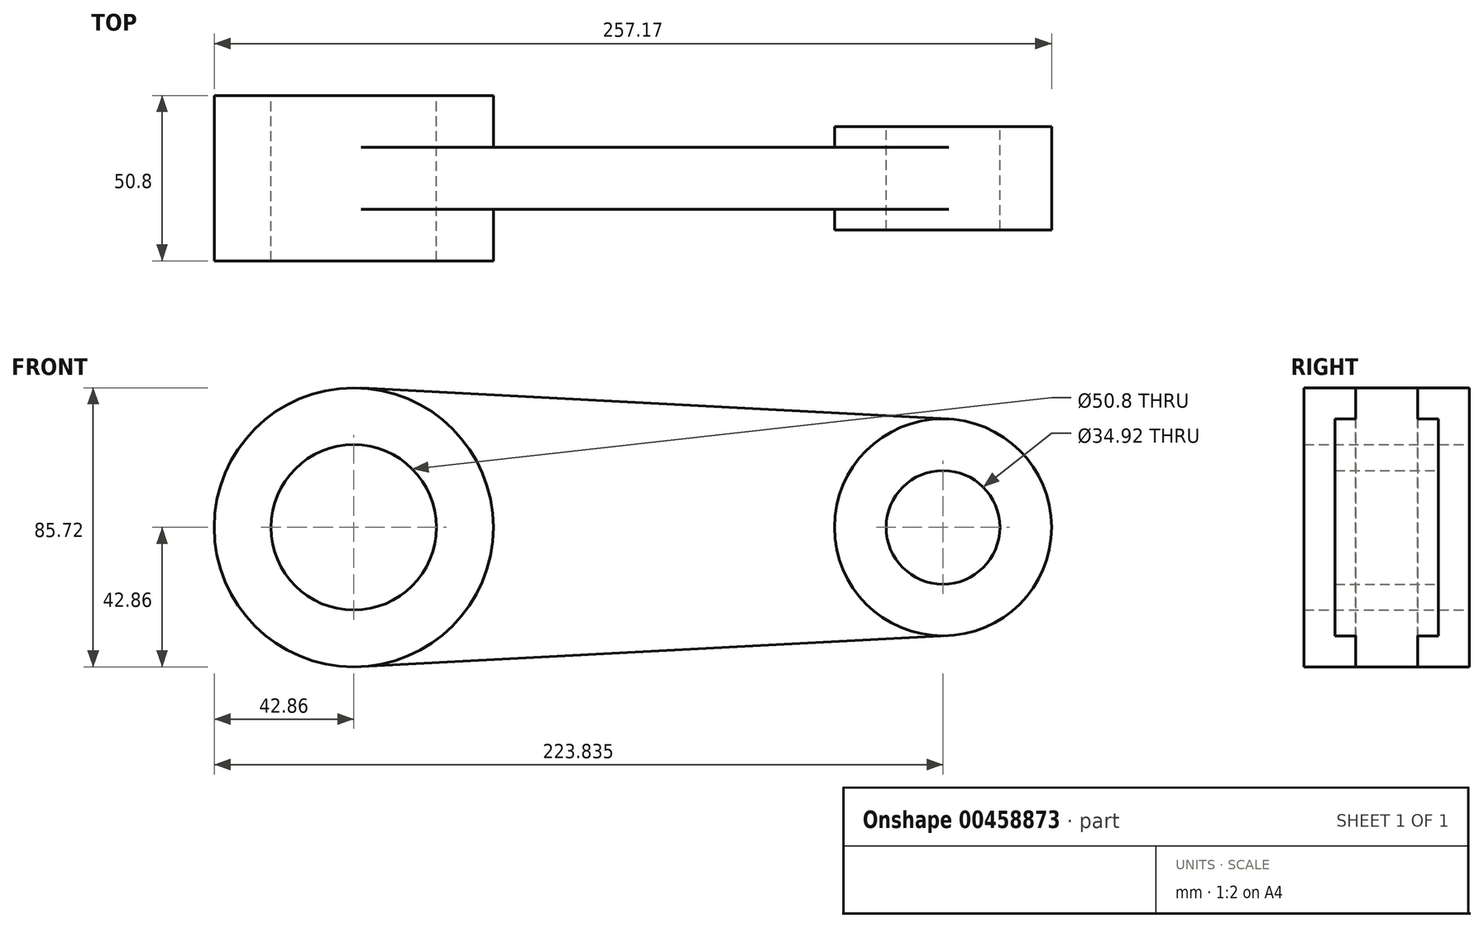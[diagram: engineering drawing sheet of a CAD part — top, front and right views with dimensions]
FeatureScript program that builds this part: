
annotation { "Feature Type Name" : "Feature", "Feature Type Description" : "" }
export const myFeature = defineFeature(function(context is Context, id is Id, definition is map)
    precondition{}
    {
        {
            var Q0;
            Q0=qCreatedBy(makeId("Front.planeOp"),FACE);
            var sketch = newSketch(context, id + "F0", { "sketchPlane" : qUnion([Q0])});
            skCircle(sketch, "E0", {"center": v(0, 0) * mm, "radius": 25.4 * mm});
            skCircle(sketch, "E1", {"center": v(0, 0) * mm, "radius": 42.86 * mm});
            skCircle(sketch, "E2", {"center": v(180.98, 0) * mm, "radius": 17.46 * mm});
            skCircle(sketch, "E3", {"center": v(180.98, 0) * mm, "radius": 33.34 * mm});
            skLineSegment(sketch, "E4", {"start": v(0, 0) * mm, "end": v(180.98, 0) * mm, "construction": true});
            skLineSegment(sketch, "E5", {"start": v(2.26, 42.8) * mm, "end": v(182.73, 33.3) * mm});
            skLineSegment(sketch, "E6.MirrorCS", {"start": v(2.26, -42.8) * mm, "end": v(182.73, -33.3) * mm});
            skSolve(sketch);
        }
        {
            var Q0;
            Q0=makeQuery(id+"F0.imprint","IMPRINT",FACE,{"disambiguationData":[TD([[makeQuery(id+"F0.imprint","IMPRINT",EDGE,{"derivedFrom":sQuery(id+"F0.wireOp",EDGE,"E0")}),-1.0]])]});
            extrude(context, id + "F1", {"entities" : qUnion([Q0]), "depth" : 50.8 * mm, "symmetric" : true});
        }
        {
            var Q0;
            {var subQ0=sQuery(id+"F0.wireOp",EDGE,"iaiyhtZe-uAdw-0OpP-Abch-S62ud13HqYB8");var subQ1=sQuery(id+"F0.wireOp",EDGE,"E1");var subQ2=makeQuery(id+"F0.imprint","INTERSECT",VERTEX,{"disambiguationData":[OD(1.0)],"derivedFrom":[subQ1,subQ0]});Q0=makeQuery(id+"F0.imprint","IMPRINT",FACE,{"disambiguationData":[TD([[makeQuery(id+"F0.imprint","IMPRINT",EDGE,{"disambiguationData":[TD([[subQ2,1.0]])],"derivedFrom":subQ1}),-1.0]])]});}
            extrude(context, id + "F2", {"entities" : qUnion([Q0]), "operationType" : NewBodyOperationType.ADD, "depth" : 19.05 * mm, "symmetric" : true});
        }
        {
            var Q0;
            Q0=makeQuery(id+"F0.imprint","IMPRINT",FACE,{"disambiguationData":[TD([[makeQuery(id+"F0.imprint","IMPRINT",EDGE,{"derivedFrom":sQuery(id+"F0.wireOp",EDGE,"E2")}),-1.0]])]});
            extrude(context, id + "F3", {"entities" : qUnion([Q0]), "operationType" : NewBodyOperationType.ADD, "depth" : 31.75 * mm, "symmetric" : true});
        }
    });
